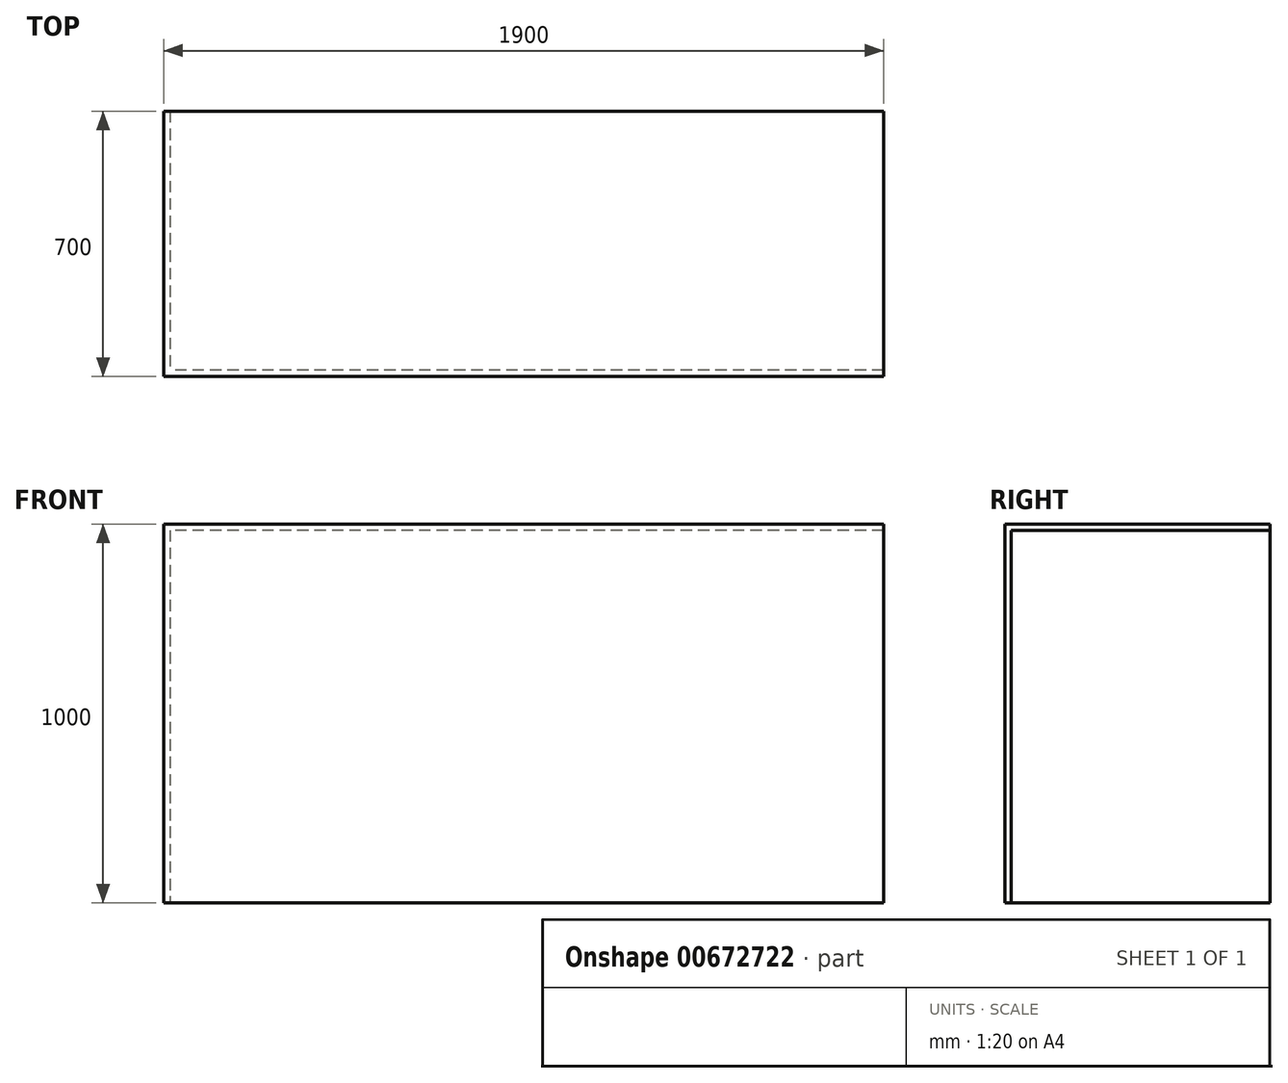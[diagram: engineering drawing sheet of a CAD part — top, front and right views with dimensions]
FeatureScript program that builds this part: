
annotation { "Feature Type Name" : "Feature", "Feature Type Description" : "" }
export const myFeature = defineFeature(function(context is Context, id is Id, definition is map)
    precondition{}
    {
        {
            var Q0;
            Q0=qCreatedBy(makeId("Top.planeOp"),FACE);
            var sketch = newSketch(context, id + "F0", { "sketchPlane" : qUnion([Q0])});
            skLineSegment(sketch, "E0.bottom", {"start": v(0, 0) * mm, "end": v(-1900, 0) * mm});
            skLineSegment(sketch, "E0.top", {"start": v(0, -700) * mm, "end": v(-1900, -700) * mm});
            skLineSegment(sketch, "E0.left", {"start": v(0, 0) * mm, "end": v(0, -700) * mm});
            skLineSegment(sketch, "E0.right", {"start": v(-1900, 0) * mm, "end": v(-1900, -700) * mm});
            skSolve(sketch);
        }
        {
            var Q0;
            Q0=makeQuery(id+"F0.imprint","IMPRINT",FACE,{"disambiguationData":[TD([[makeQuery(id+"F0.imprint","IMPRINT",EDGE,{"derivedFrom":sQuery(id+"F0.wireOp",EDGE,"Y66rWitT-qBWe-ztKi-yuPp-pPcdfemAuZkT.bottom")}),-1.0]])]});
            var Q1;
            Q1=makeQuery(id+"F0.imprint","IMPRINT",FACE,{"disambiguationData":[TD([[makeQuery(id+"F0.imprint","IMPRINT",EDGE,{"derivedFrom":sQuery(id+"F0.wireOp",EDGE,"E0.bottom")}),1.0]])]});
            extrude(context, id + "F1", {"entities" : qUnion([Q0, Q1]), "depth" : 1000 * mm, "offsetDistance" : 25 * mm});
        }
        {
            var Q0;
            Q0=makeQuery(id+"F1.opExtrude","CAP_FACE",FACE,{"disambiguationData":[OSD([sQuery(id+"F0.wireOp",EDGE,"E0.bottom"),sQuery(id+"F0.wireOp",EDGE,"E0.top"),sQuery(id+"F0.wireOp",EDGE,"E0.left"),sQuery(id+"F0.wireOp",EDGE,"E0.right")])],"isStart":true});
            var Q1;
            Q1=makeQuery(id+"F1.opExtrude","SWEPT_FACE",FACE,{"disambiguationData":[OSD([sQuery(id+"F0.wireOp",EDGE,"E0.left")])]});
            var Q2;
            Q2=makeQuery(id+"F1.opExtrude","SWEPT_FACE",FACE,{"disambiguationData":[OSD([sQuery(id+"F0.wireOp",EDGE,"E0.bottom")])]});
            shell(context, id + "F2", {"entities" : qUnion([Q0, Q1, Q2]), "thickness" : 16 * mm});
        }
    });
